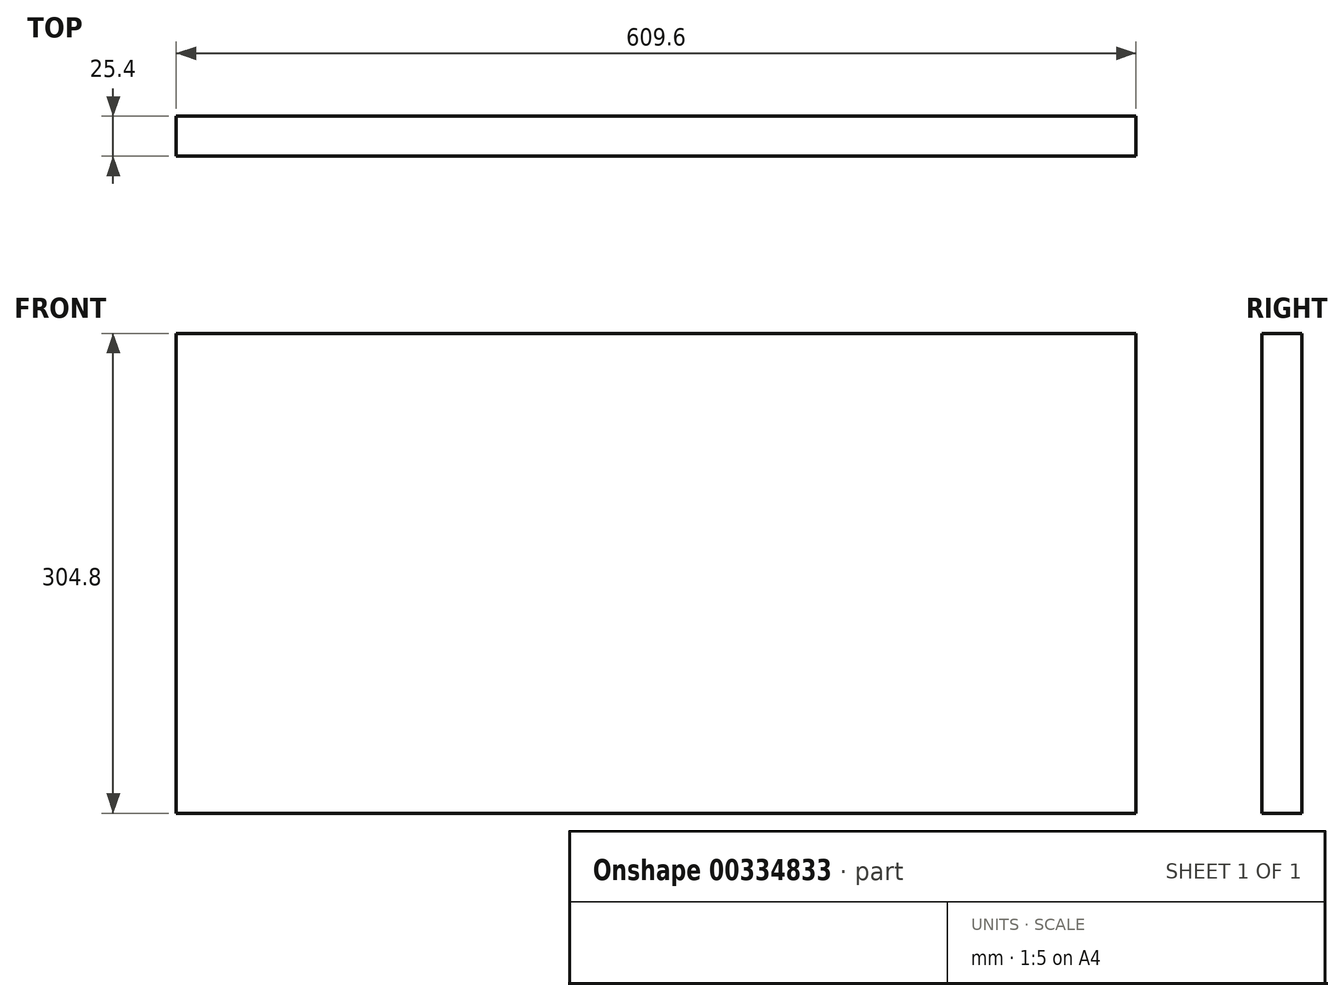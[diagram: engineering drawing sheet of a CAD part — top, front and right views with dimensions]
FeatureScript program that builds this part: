
annotation { "Feature Type Name" : "Feature", "Feature Type Description" : "" }
export const myFeature = defineFeature(function(context is Context, id is Id, definition is map)
    precondition{}
    {
        {
            var Q0;
            Q0=qCreatedBy(makeId("Front.planeOp"),FACE);
            var sketch = newSketch(context, id + "F0", { "sketchPlane" : qUnion([Q0])});
            skLineSegment(sketch, "E0.bottom", {"start": v(-290.19, 304.8) * mm, "end": v(319.41, 304.8) * mm});
            skLineSegment(sketch, "E0.top", {"start": v(-290.19, 0) * mm, "end": v(319.41, 0) * mm});
            skLineSegment(sketch, "E0.left", {"start": v(-290.19, 304.8) * mm, "end": v(-290.19, 0) * mm});
            skLineSegment(sketch, "E0.right", {"start": v(319.41, 304.8) * mm, "end": v(319.41, 0) * mm});
            skSolve(sketch);
        }
        {
            var Q0;
            Q0=makeQuery(id+"F0.imprint","IMPRINT",FACE,{"disambiguationData":[TD([[makeQuery(id+"F0.imprint","IMPRINT",EDGE,{"derivedFrom":sQuery(id+"F0.wireOp",EDGE,"E0.bottom")}),-1.0]])]});
            extrude(context, id + "F1", {"entities" : qUnion([Q0]), "depth" : 25.4 * mm});
        }
    });
